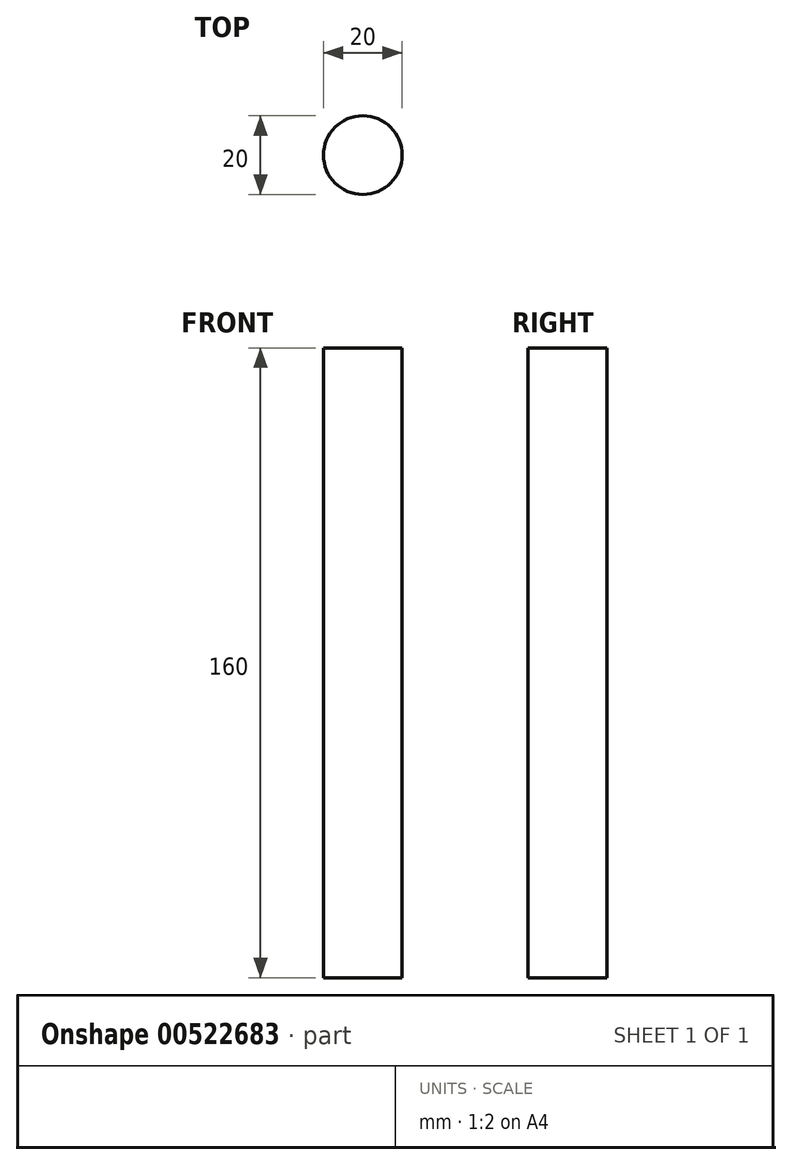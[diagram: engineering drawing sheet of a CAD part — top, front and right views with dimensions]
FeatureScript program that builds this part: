
annotation { "Feature Type Name" : "Feature", "Feature Type Description" : "" }
export const myFeature = defineFeature(function(context is Context, id is Id, definition is map)
    precondition{}
    {
        {
            var Q0;
            Q0=qCreatedBy(makeId("Top.planeOp"),FACE);
            var sketch = newSketch(context, id + "F0", { "sketchPlane" : qUnion([Q0])});
            skCircle(sketch, "E0", {"center": v(0, 0) * mm, "radius": 10 * mm});
            skSolve(sketch);
        }
        {
            var Q0;
            Q0=makeQuery(id+"F0.imprint","IMPRINT",FACE,{"disambiguationData":[TD([[makeQuery(id+"F0.imprint","IMPRINT",EDGE,{"derivedFrom":sQuery(id+"F0.wireOp",EDGE,"E0")}),1.0]])]});
            extrude(context, id + "F1", {"entities" : qUnion([Q0]), "depth" : 160 * mm, "offsetDistance" : 25 * mm});
        }
    });
